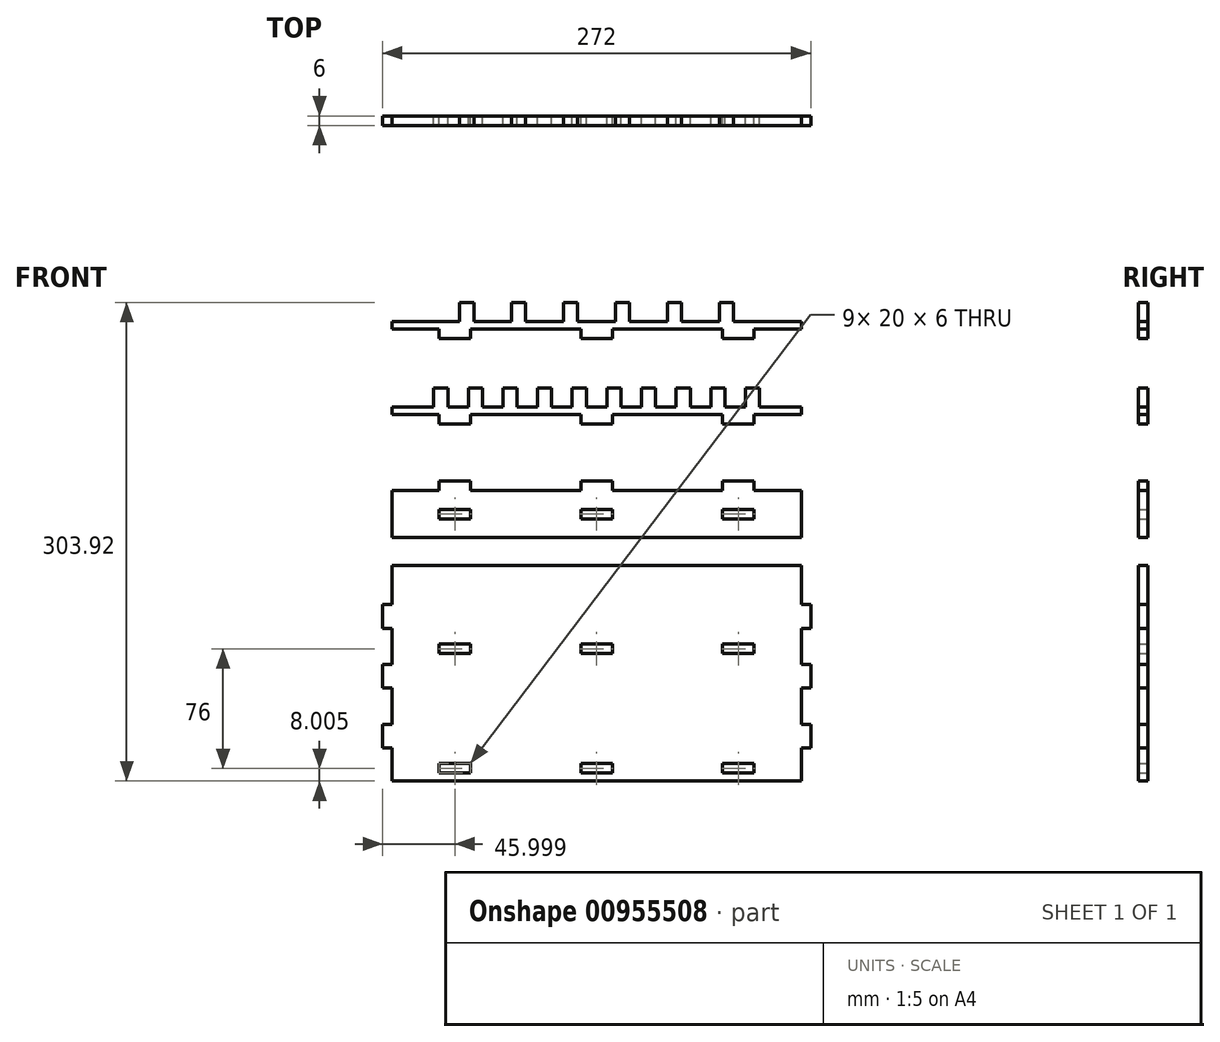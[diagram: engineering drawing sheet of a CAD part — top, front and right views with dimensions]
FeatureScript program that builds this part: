
annotation { "Feature Type Name" : "Feature", "Feature Type Description" : "" }
export const myFeature = defineFeature(function(context is Context, id is Id, definition is map)
    precondition{}
    {
        {
            var Q0;
            Q0=qCreatedBy(makeId("Front.planeOp"),FACE);
            var sketch = newSketch(context, id + "F0", { "sketchPlane" : qUnion([Q0])});
            skLineSegment(sketch, "E0", {"start": v(-63.3, 14.61) * mm, "end": v(-63.3, 26.61) * mm});
            skLineSegment(sketch, "E1", {"start": v(-63.3, 26.61) * mm, "end": v(-54.3, 26.61) * mm});
            skLineSegment(sketch, "E2", {"start": v(-54.3, 26.61) * mm, "end": v(-54.3, 14.61) * mm});
            skLineSegment(sketch, "E3", {"start": v(-54.3, 14.61) * mm, "end": v(-30.3, 14.61) * mm});
            skLineSegment(sketch, "E4.1.0.0", {"start": v(-30.3, 14.61) * mm, "end": v(-30.3, 26.61) * mm});
            skLineSegment(sketch, "E4.1.0.1", {"start": v(-30.3, 26.61) * mm, "end": v(-21.3, 26.61) * mm});
            skLineSegment(sketch, "E4.1.0.2", {"start": v(-21.3, 26.61) * mm, "end": v(-21.3, 14.61) * mm});
            skLineSegment(sketch, "E4.1.0.3", {"start": v(-21.3, 14.61) * mm, "end": v(2.7, 14.61) * mm});
            skLineSegment(sketch, "E4.2.0.0", {"start": v(2.7, 14.61) * mm, "end": v(2.7, 26.61) * mm});
            skLineSegment(sketch, "E4.2.0.1", {"start": v(2.7, 26.61) * mm, "end": v(11.7, 26.61) * mm});
            skLineSegment(sketch, "E4.2.0.2", {"start": v(11.7, 26.61) * mm, "end": v(11.7, 14.61) * mm});
            skLineSegment(sketch, "E4.2.0.3", {"start": v(11.7, 14.61) * mm, "end": v(35.7, 14.61) * mm});
            skLineSegment(sketch, "E4.3.0.0", {"start": v(35.7, 14.61) * mm, "end": v(35.7, 26.61) * mm});
            skLineSegment(sketch, "E4.3.0.1", {"start": v(35.7, 26.61) * mm, "end": v(44.7, 26.61) * mm});
            skLineSegment(sketch, "E4.3.0.2", {"start": v(44.7, 26.61) * mm, "end": v(44.7, 14.61) * mm});
            skLineSegment(sketch, "E4.direction1", {"start": v(-63.3, 14.61) * mm, "end": v(-30.3, 14.61) * mm, "construction": true});
            skLineSegment(sketch, "E5", {"start": v(-79.8, -39.65) * mm, "end": v(-79.8, -27.65) * mm});
            skLineSegment(sketch, "E6", {"start": v(-79.8, -27.65) * mm, "end": v(-70.8, -27.65) * mm});
            skLineSegment(sketch, "E7", {"start": v(-70.8, -27.65) * mm, "end": v(-70.8, -39.65) * mm});
            skLineSegment(sketch, "E8", {"start": v(-70.8, -39.65) * mm, "end": v(-57.8, -39.65) * mm});
            skLineSegment(sketch, "E9.1.0.0", {"start": v(-57.8, -39.65) * mm, "end": v(-57.8, -27.65) * mm});
            skLineSegment(sketch, "E9.1.0.1", {"start": v(-57.8, -27.65) * mm, "end": v(-48.8, -27.65) * mm});
            skLineSegment(sketch, "E9.1.0.2", {"start": v(-48.8, -27.65) * mm, "end": v(-48.8, -39.65) * mm});
            skLineSegment(sketch, "E9.1.0.3", {"start": v(-48.8, -39.65) * mm, "end": v(-35.8, -39.65) * mm});
            skLineSegment(sketch, "E9.2.0.0", {"start": v(-35.8, -39.65) * mm, "end": v(-35.8, -27.65) * mm});
            skLineSegment(sketch, "E9.2.0.1", {"start": v(-35.8, -27.65) * mm, "end": v(-26.8, -27.65) * mm});
            skLineSegment(sketch, "E9.2.0.2", {"start": v(-26.8, -27.65) * mm, "end": v(-26.8, -39.65) * mm});
            skLineSegment(sketch, "E9.2.0.3", {"start": v(-26.8, -39.65) * mm, "end": v(-13.8, -39.65) * mm});
            skLineSegment(sketch, "E9.direction1", {"start": v(-79.8, -39.65) * mm, "end": v(-57.8, -39.65) * mm, "construction": true});
            skLineSegment(sketch, "E10", {"start": v(-63.3, 14.61) * mm, "end": v(-106.3, 14.61) * mm});
            skLineSegment(sketch, "E11", {"start": v(-106.3, 14.61) * mm, "end": v(-106.3, 9.61) * mm});
            skLineSegment(sketch, "E12", {"start": v(-106.3, 9.61) * mm, "end": v(-76.3, 9.61) * mm});
            skLineSegment(sketch, "E13", {"start": v(-79.8, -39.65) * mm, "end": v(-106.3, -39.65) * mm});
            skLineSegment(sketch, "E14", {"start": v(-106.3, -39.65) * mm, "end": v(-106.3, -44.65) * mm});
            skLineSegment(sketch, "E15", {"start": v(-106.3, -44.65) * mm, "end": v(-76.3, -44.65) * mm});
            skLineSegment(sketch, "E16.top", {"start": v(-76.3, 3.61) * mm, "end": v(-56.3, 3.61) * mm});
            skLineSegment(sketch, "E16.left", {"start": v(-76.3, 9.61) * mm, "end": v(-76.3, 3.61) * mm});
            skLineSegment(sketch, "E16.right", {"start": v(-56.3, 9.61) * mm, "end": v(-56.3, 3.61) * mm});
            skLineSegment(sketch, "E17.top", {"start": v(-76.3, -50.65) * mm, "end": v(-56.3, -50.65) * mm});
            skLineSegment(sketch, "E17.left", {"start": v(-76.3, -44.65) * mm, "end": v(-76.3, -50.65) * mm});
            skLineSegment(sketch, "E17.right", {"start": v(-56.3, -44.65) * mm, "end": v(-56.3, -50.65) * mm});
            skLineSegment(sketch, "E18.1.0.0", {"start": v(13.7, 9.61) * mm, "end": v(13.7, 3.61) * mm});
            skLineSegment(sketch, "E18.1.0.1", {"start": v(13.7, 3.61) * mm, "end": v(33.7, 3.61) * mm});
            skLineSegment(sketch, "E18.1.0.2", {"start": v(33.7, 9.61) * mm, "end": v(33.7, 3.61) * mm});
            skLineSegment(sketch, "E18.2.0.0", {"start": v(103.7, 9.61) * mm, "end": v(103.7, 3.61) * mm});
            skLineSegment(sketch, "E18.2.0.1", {"start": v(103.7, 3.61) * mm, "end": v(123.7, 3.61) * mm});
            skLineSegment(sketch, "E18.2.0.2", {"start": v(123.7, 9.61) * mm, "end": v(123.7, 3.61) * mm});
            skLineSegment(sketch, "E18.direction1", {"start": v(-76.3, 3.61) * mm, "end": v(13.7, 3.61) * mm, "construction": true});
            skLineSegment(sketch, "E19.1.0.0", {"start": v(13.7, -44.65) * mm, "end": v(13.7, -50.65) * mm});
            skLineSegment(sketch, "E19.1.0.1", {"start": v(13.7, -50.65) * mm, "end": v(33.7, -50.65) * mm});
            skLineSegment(sketch, "E19.1.0.2", {"start": v(33.7, -44.65) * mm, "end": v(33.7, -50.65) * mm});
            skLineSegment(sketch, "E19.2.0.0", {"start": v(103.7, -44.65) * mm, "end": v(103.7, -50.65) * mm});
            skLineSegment(sketch, "E19.2.0.1", {"start": v(103.7, -50.65) * mm, "end": v(123.7, -50.65) * mm});
            skLineSegment(sketch, "E19.2.0.2", {"start": v(123.7, -44.65) * mm, "end": v(123.7, -50.65) * mm});
            skLineSegment(sketch, "E19.direction1", {"start": v(-76.3, -50.65) * mm, "end": v(13.7, -50.65) * mm, "construction": true});
            skLineSegment(sketch, "E20.trimOffspring", {"start": v(-56.3, 9.61) * mm, "end": v(13.7, 9.61) * mm});
            skLineSegment(sketch, "E21.trimOffspring", {"start": v(33.7, 9.61) * mm, "end": v(103.7, 9.61) * mm});
            skLineSegment(sketch, "E22.trimOffspring", {"start": v(33.7, -44.65) * mm, "end": v(103.7, -44.65) * mm});
            skLineSegment(sketch, "E23.trimOffspring", {"start": v(-56.3, -44.65) * mm, "end": v(13.7, -44.65) * mm});
            skLineSegment(sketch, "E24.bottom", {"start": v(-106.3, -92.77) * mm, "end": v(-76.3, -92.77) * mm});
            skLineSegment(sketch, "E24.top", {"start": v(-106.3, -122.77) * mm, "end": v(153.7, -122.77) * mm});
            skLineSegment(sketch, "E24.left", {"start": v(-106.3, -92.77) * mm, "end": v(-106.3, -122.77) * mm});
            skLineSegment(sketch, "E24.right", {"start": v(153.7, -92.77) * mm, "end": v(153.7, -122.77) * mm});
            skLineSegment(sketch, "E25", {"start": v(-106.3, -107.77) * mm, "end": v(153.7, -107.77) * mm, "construction": true});
            skLineSegment(sketch, "E26.bottom", {"start": v(-76.3, -104.77) * mm, "end": v(-56.3, -104.77) * mm});
            skLineSegment(sketch, "E26.top", {"start": v(-76.3, -110.77) * mm, "end": v(-56.3, -110.77) * mm});
            skLineSegment(sketch, "E26.left", {"start": v(-76.3, -104.77) * mm, "end": v(-76.3, -110.77) * mm});
            skLineSegment(sketch, "E26.right", {"start": v(-56.3, -104.77) * mm, "end": v(-56.3, -110.77) * mm});
            skPoint(sketch, "E26.middle", {"position": v(-66.3, -107.77) * mm});
            skLineSegment(sketch, "E27.1.0.0", {"start": v(13.7, -104.77) * mm, "end": v(33.7, -104.77) * mm});
            skLineSegment(sketch, "E27.1.0.1", {"start": v(13.7, -104.77) * mm, "end": v(13.7, -110.77) * mm});
            skLineSegment(sketch, "E27.1.0.2", {"start": v(13.7, -110.77) * mm, "end": v(33.7, -110.77) * mm});
            skLineSegment(sketch, "E27.1.0.3", {"start": v(33.7, -104.77) * mm, "end": v(33.7, -110.77) * mm});
            skLineSegment(sketch, "E27.2.0.0", {"start": v(103.7, -104.77) * mm, "end": v(123.7, -104.77) * mm});
            skLineSegment(sketch, "E27.2.0.1", {"start": v(103.7, -104.77) * mm, "end": v(103.7, -110.77) * mm});
            skLineSegment(sketch, "E27.2.0.2", {"start": v(103.7, -110.77) * mm, "end": v(123.7, -110.77) * mm});
            skLineSegment(sketch, "E27.2.0.3", {"start": v(123.7, -104.77) * mm, "end": v(123.7, -110.77) * mm});
            skLineSegment(sketch, "E27.direction1", {"start": v(-76.3, -104.77) * mm, "end": v(13.7, -104.77) * mm, "construction": true});
            skLineSegment(sketch, "E28.top", {"start": v(-76.3, -86.77) * mm, "end": v(-56.3, -86.77) * mm});
            skLineSegment(sketch, "E28.left", {"start": v(-76.3, -92.77) * mm, "end": v(-76.3, -86.77) * mm});
            skLineSegment(sketch, "E28.right", {"start": v(-56.3, -92.77) * mm, "end": v(-56.3, -86.77) * mm});
            skLineSegment(sketch, "E29.trimOffspring", {"start": v(-56.3, -92.77) * mm, "end": v(13.7, -92.77) * mm});
            skLineSegment(sketch, "E30.bottom", {"start": v(-106.3, -140.3) * mm, "end": v(153.7, -140.3) * mm});
            skLineSegment(sketch, "E30.top", {"start": v(-106.3, -277.3) * mm, "end": v(153.7, -277.3) * mm});
            skLineSegment(sketch, "E30.left", {"start": v(-106.3, -140.3) * mm, "end": v(-106.3, -165.3) * mm});
            skLineSegment(sketch, "E30.right", {"start": v(153.7, -140.3) * mm, "end": v(153.7, -165.3) * mm});
            skLineSegment(sketch, "E31", {"start": v(-106.3, -193.3) * mm, "end": v(153.7, -193.3) * mm, "construction": true});
            skLineSegment(sketch, "E32", {"start": v(-106.3, -269.3) * mm, "end": v(153.7, -269.3) * mm, "construction": true});
            skLineSegment(sketch, "E33.bottom", {"start": v(-56.3, -196.3) * mm, "end": v(-76.3, -196.3) * mm});
            skLineSegment(sketch, "E33.top", {"start": v(-56.3, -190.3) * mm, "end": v(-76.3, -190.3) * mm});
            skLineSegment(sketch, "E33.left", {"start": v(-56.3, -196.3) * mm, "end": v(-56.3, -190.3) * mm});
            skLineSegment(sketch, "E33.right", {"start": v(-76.3, -196.3) * mm, "end": v(-76.3, -190.3) * mm});
            skPoint(sketch, "E33.middle", {"position": v(-66.3, -193.3) * mm});
            skLineSegment(sketch, "E34.bottom", {"start": v(-56.3, -266.3) * mm, "end": v(-76.3, -266.3) * mm});
            skLineSegment(sketch, "E34.top", {"start": v(-56.3, -272.3) * mm, "end": v(-76.3, -272.3) * mm});
            skLineSegment(sketch, "E34.left", {"start": v(-56.3, -266.3) * mm, "end": v(-56.3, -272.3) * mm});
            skLineSegment(sketch, "E34.right", {"start": v(-76.3, -266.3) * mm, "end": v(-76.3, -272.3) * mm});
            skPoint(sketch, "E34.middle", {"position": v(-66.3, -269.3) * mm});
            skLineSegment(sketch, "E35.1.0.0", {"start": v(33.7, -190.3) * mm, "end": v(13.7, -190.3) * mm});
            skLineSegment(sketch, "E35.1.0.1", {"start": v(13.7, -196.3) * mm, "end": v(13.7, -190.3) * mm});
            skLineSegment(sketch, "E35.1.0.2", {"start": v(33.7, -196.3) * mm, "end": v(13.7, -196.3) * mm});
            skLineSegment(sketch, "E35.1.0.3", {"start": v(33.7, -196.3) * mm, "end": v(33.7, -190.3) * mm});
            skLineSegment(sketch, "E35.2.0.0", {"start": v(123.7, -190.3) * mm, "end": v(103.7, -190.3) * mm});
            skLineSegment(sketch, "E35.2.0.1", {"start": v(103.7, -196.3) * mm, "end": v(103.7, -190.3) * mm});
            skLineSegment(sketch, "E35.2.0.2", {"start": v(123.7, -196.3) * mm, "end": v(103.7, -196.3) * mm});
            skLineSegment(sketch, "E35.2.0.3", {"start": v(123.7, -196.3) * mm, "end": v(123.7, -190.3) * mm});
            skLineSegment(sketch, "E35.direction1", {"start": v(-76.3, -190.3) * mm, "end": v(13.7, -190.3) * mm, "construction": true});
            skLineSegment(sketch, "E36.1.0.0", {"start": v(13.7, -266.3) * mm, "end": v(13.7, -272.3) * mm});
            skLineSegment(sketch, "E36.1.0.1", {"start": v(33.7, -266.3) * mm, "end": v(13.7, -266.3) * mm});
            skLineSegment(sketch, "E36.1.0.2", {"start": v(33.7, -266.3) * mm, "end": v(33.7, -272.3) * mm});
            skLineSegment(sketch, "E36.1.0.3", {"start": v(33.7, -272.3) * mm, "end": v(13.7, -272.3) * mm});
            skLineSegment(sketch, "E36.2.0.0", {"start": v(103.7, -266.3) * mm, "end": v(103.7, -272.3) * mm});
            skLineSegment(sketch, "E36.2.0.1", {"start": v(123.7, -266.3) * mm, "end": v(103.7, -266.3) * mm});
            skLineSegment(sketch, "E36.2.0.2", {"start": v(123.7, -266.3) * mm, "end": v(123.7, -272.3) * mm});
            skLineSegment(sketch, "E36.2.0.3", {"start": v(123.7, -272.3) * mm, "end": v(103.7, -272.3) * mm});
            skLineSegment(sketch, "E36.direction1", {"start": v(-76.3, -272.3) * mm, "end": v(13.7, -272.3) * mm, "construction": true});
            skLineSegment(sketch, "E37.bottom", {"start": v(-106.3, -165.3) * mm, "end": v(-112.3, -165.3) * mm});
            skLineSegment(sketch, "E37.top", {"start": v(-106.3, -180.3) * mm, "end": v(-112.3, -180.3) * mm});
            skLineSegment(sketch, "E37.right", {"start": v(-112.3, -165.3) * mm, "end": v(-112.3, -180.3) * mm});
            skLineSegment(sketch, "E38.0.1.0", {"start": v(-106.3, -203.3) * mm, "end": v(-112.3, -203.3) * mm});
            skLineSegment(sketch, "E38.0.1.2", {"start": v(-106.3, -218.3) * mm, "end": v(-112.3, -218.3) * mm});
            skLineSegment(sketch, "E38.0.1.3", {"start": v(-112.3, -203.3) * mm, "end": v(-112.3, -218.3) * mm});
            skLineSegment(sketch, "E38.1.0.0", {"start": v(159.7, -165.3) * mm, "end": v(153.7, -165.3) * mm});
            skLineSegment(sketch, "E38.1.0.1", {"start": v(159.7, -165.3) * mm, "end": v(159.7, -180.3) * mm});
            skLineSegment(sketch, "E38.1.0.2", {"start": v(159.7, -180.3) * mm, "end": v(153.7, -180.3) * mm});
            skLineSegment(sketch, "E38.1.1.0", {"start": v(159.7, -203.3) * mm, "end": v(153.7, -203.3) * mm});
            skLineSegment(sketch, "E38.1.1.1", {"start": v(159.7, -203.3) * mm, "end": v(159.7, -218.3) * mm});
            skLineSegment(sketch, "E38.1.1.2", {"start": v(159.7, -218.3) * mm, "end": v(153.7, -218.3) * mm});
            skLineSegment(sketch, "E38.direction1", {"start": v(-112.3, -165.3) * mm, "end": v(153.7, -165.3) * mm, "construction": true});
            skLineSegment(sketch, "E38.direction2", {"start": v(-112.3, -165.3) * mm, "end": v(-112.3, -203.3) * mm, "construction": true});
            skLineSegment(sketch, "E39.trimOffspring", {"start": v(-106.3, -218.3) * mm, "end": v(-106.3, -241.3) * mm});
            skLineSegment(sketch, "E40.trimOffspring", {"start": v(153.7, -180.3) * mm, "end": v(153.7, -203.3) * mm});
            skLineSegment(sketch, "E41.trimOffspring", {"start": v(153.7, -218.3) * mm, "end": v(153.7, -241.3) * mm});
            skLineSegment(sketch, "E42.trimOffspring", {"start": v(-106.3, -180.3) * mm, "end": v(-106.3, -203.3) * mm});
            skLineSegment(sketch, "E43.0.3.0", {"start": v(-13.8, -39.65) * mm, "end": v(-13.8, -27.65) * mm});
            skLineSegment(sketch, "E43.3.3.0", {"start": v(-13.8, -27.65) * mm, "end": v(-4.8, -27.65) * mm});
            skLineSegment(sketch, "E43.6.3.0", {"start": v(-4.8, -27.65) * mm, "end": v(-4.8, -39.65) * mm});
            skLineSegment(sketch, "E43.9.3.0", {"start": v(-4.8, -39.65) * mm, "end": v(8.2, -39.65) * mm});
            skLineSegment(sketch, "E43.0.4.0", {"start": v(8.2, -39.65) * mm, "end": v(8.2, -27.65) * mm});
            skLineSegment(sketch, "E43.3.4.0", {"start": v(8.2, -27.65) * mm, "end": v(17.2, -27.65) * mm});
            skLineSegment(sketch, "E43.6.4.0", {"start": v(17.2, -27.65) * mm, "end": v(17.2, -39.65) * mm});
            skLineSegment(sketch, "E43.9.4.0", {"start": v(17.2, -39.65) * mm, "end": v(30.2, -39.65) * mm});
            skLineSegment(sketch, "E43.0.5.0", {"start": v(30.2, -39.65) * mm, "end": v(30.2, -27.65) * mm});
            skLineSegment(sketch, "E43.3.5.0", {"start": v(30.2, -27.65) * mm, "end": v(39.2, -27.65) * mm});
            skLineSegment(sketch, "E43.6.5.0", {"start": v(39.2, -27.65) * mm, "end": v(39.2, -39.65) * mm});
            skLineSegment(sketch, "E43.9.5.0", {"start": v(39.2, -39.65) * mm, "end": v(52.2, -39.65) * mm});
            skLineSegment(sketch, "E43.0.6.0", {"start": v(52.2, -39.65) * mm, "end": v(52.2, -27.65) * mm});
            skLineSegment(sketch, "E43.3.6.0", {"start": v(52.2, -27.65) * mm, "end": v(61.2, -27.65) * mm});
            skLineSegment(sketch, "E43.6.6.0", {"start": v(61.2, -27.65) * mm, "end": v(61.2, -39.65) * mm});
            skLineSegment(sketch, "E44", {"start": v(123.7, -44.65) * mm, "end": v(153.7, -44.65) * mm});
            skLineSegment(sketch, "E45", {"start": v(153.7, -44.65) * mm, "end": v(153.7, -39.65) * mm});
            skLineSegment(sketch, "E46", {"start": v(153.7, 14.61) * mm, "end": v(153.7, 9.61) * mm});
            skLineSegment(sketch, "E47", {"start": v(153.7, 9.61) * mm, "end": v(123.7, 9.61) * mm});
            skLineSegment(sketch, "E48.1.0.0", {"start": v(13.7, -92.77) * mm, "end": v(13.7, -86.77) * mm});
            skLineSegment(sketch, "E48.1.0.1", {"start": v(13.7, -86.77) * mm, "end": v(33.7, -86.77) * mm});
            skLineSegment(sketch, "E48.1.0.2", {"start": v(33.7, -92.77) * mm, "end": v(33.7, -86.77) * mm});
            skLineSegment(sketch, "E48.2.0.0", {"start": v(103.7, -92.77) * mm, "end": v(103.7, -86.77) * mm});
            skLineSegment(sketch, "E48.2.0.1", {"start": v(103.7, -86.77) * mm, "end": v(123.7, -86.77) * mm});
            skLineSegment(sketch, "E48.2.0.2", {"start": v(123.7, -92.77) * mm, "end": v(123.7, -86.77) * mm});
            skLineSegment(sketch, "E48.direction1", {"start": v(-76.3, -92.77) * mm, "end": v(13.7, -92.77) * mm, "construction": true});
            skLineSegment(sketch, "E49.trimOffspring", {"start": v(33.7, -92.77) * mm, "end": v(103.7, -92.77) * mm});
            skLineSegment(sketch, "E50.trimOffspring", {"start": v(123.7, -92.77) * mm, "end": v(153.7, -92.77) * mm});
            skLineSegment(sketch, "E51.0.4.0", {"start": v(68.7, 14.61) * mm, "end": v(68.7, 26.61) * mm});
            skLineSegment(sketch, "E51.3.4.0", {"start": v(68.7, 26.61) * mm, "end": v(77.7, 26.61) * mm});
            skLineSegment(sketch, "E51.6.4.0", {"start": v(77.7, 26.61) * mm, "end": v(77.7, 14.61) * mm});
            skLineSegment(sketch, "E51.9.4.0", {"start": v(77.7, 14.61) * mm, "end": v(101.7, 14.61) * mm});
            skLineSegment(sketch, "E51.0.5.0", {"start": v(101.7, 14.61) * mm, "end": v(101.7, 26.61) * mm});
            skLineSegment(sketch, "E51.3.5.0", {"start": v(101.7, 26.61) * mm, "end": v(110.7, 26.61) * mm});
            skLineSegment(sketch, "E51.6.5.0", {"start": v(110.7, 26.61) * mm, "end": v(110.7, 14.61) * mm});
            skLineSegment(sketch, "E51.9.5.0", {"start": v(110.7, 14.61) * mm, "end": v(134.7, 14.61) * mm});
            skLineSegment(sketch, "E52.0.7.0", {"start": v(74.2, -39.65) * mm, "end": v(74.2, -27.65) * mm});
            skLineSegment(sketch, "E52.3.7.0", {"start": v(74.2, -27.65) * mm, "end": v(83.2, -27.65) * mm});
            skLineSegment(sketch, "E52.6.7.0", {"start": v(83.2, -27.65) * mm, "end": v(83.2, -39.65) * mm});
            skLineSegment(sketch, "E52.9.7.0", {"start": v(83.2, -39.65) * mm, "end": v(96.2, -39.65) * mm});
            skLineSegment(sketch, "E52.0.8.0", {"start": v(96.2, -39.65) * mm, "end": v(96.2, -27.65) * mm});
            skLineSegment(sketch, "E52.3.8.0", {"start": v(96.2, -27.65) * mm, "end": v(105.2, -27.65) * mm});
            skLineSegment(sketch, "E52.6.8.0", {"start": v(105.2, -27.65) * mm, "end": v(105.2, -39.65) * mm});
            skLineSegment(sketch, "E52.9.8.0", {"start": v(105.2, -39.65) * mm, "end": v(118.2, -39.65) * mm});
            skLineSegment(sketch, "E52.0.9.0", {"start": v(118.2, -39.65) * mm, "end": v(118.2, -27.65) * mm});
            skLineSegment(sketch, "E52.3.9.0", {"start": v(118.2, -27.65) * mm, "end": v(127.2, -27.65) * mm});
            skLineSegment(sketch, "E52.6.9.0", {"start": v(127.2, -27.65) * mm, "end": v(127.2, -39.65) * mm});
            skLineSegment(sketch, "E52.9.9.0", {"start": v(127.2, -39.65) * mm, "end": v(140.2, -39.65) * mm});
            skLineSegment(sketch, "E53", {"start": v(134.7, 14.61) * mm, "end": v(153.7, 14.61) * mm});
            skLineSegment(sketch, "E54", {"start": v(140.2, -39.65) * mm, "end": v(153.7, -39.65) * mm});
            skLineSegment(sketch, "E55", {"start": v(44.7, 14.61) * mm, "end": v(68.7, 14.61) * mm});
            skLineSegment(sketch, "E56", {"start": v(61.2, -39.65) * mm, "end": v(74.2, -39.65) * mm});
            skLineSegment(sketch, "E57.0.0.2", {"start": v(-106.3, -241.3) * mm, "end": v(-112.3, -241.3) * mm});
            skLineSegment(sketch, "E57.6.0.2", {"start": v(-106.3, -256.3) * mm, "end": v(-112.3, -256.3) * mm});
            skLineSegment(sketch, "E57.9.0.2", {"start": v(-112.3, -241.3) * mm, "end": v(-112.3, -256.3) * mm});
            skLineSegment(sketch, "E57.0.1.2", {"start": v(159.7, -241.3) * mm, "end": v(153.7, -241.3) * mm});
            skLineSegment(sketch, "E57.3.1.2", {"start": v(159.7, -241.3) * mm, "end": v(159.7, -256.3) * mm});
            skLineSegment(sketch, "E57.6.1.2", {"start": v(159.7, -256.3) * mm, "end": v(153.7, -256.3) * mm});
            skLineSegment(sketch, "E58.trimOffspring", {"start": v(-106.3, -256.3) * mm, "end": v(-106.3, -277.3) * mm});
            skLineSegment(sketch, "E59.trimOffspring", {"start": v(153.7, -256.3) * mm, "end": v(153.7, -277.3) * mm});
            skSolve(sketch);
        }
        {
            var Q0;
            Q0=makeQuery(id+"F0.imprint","IMPRINT",FACE,{"disambiguationData":[TD([[makeQuery(id+"F0.imprint","IMPRINT",EDGE,{"derivedFrom":sQuery(id+"F0.wireOp",EDGE,"E30.bottom")}),-1.0]])]});
            extrude(context, id + "F1", {"entities" : qUnion([Q0]), "depth" : 6 * mm, "offsetDistance" : 25 * mm});
        }
        {
            var Q0;
            Q0=makeQuery(id+"F0.imprint","IMPRINT",FACE,{"disambiguationData":[TD([[makeQuery(id+"F0.imprint","IMPRINT",EDGE,{"derivedFrom":sQuery(id+"F0.wireOp",EDGE,"E24.bottom")}),-1.0]])]});
            extrude(context, id + "F2", {"entities" : qUnion([Q0]), "depth" : 6 * mm, "offsetDistance" : 25 * mm});
        }
        {
            var Q0;
            Q0=makeQuery(id+"F0.imprint","IMPRINT",FACE,{"disambiguationData":[TD([[makeQuery(id+"F0.imprint","IMPRINT",EDGE,{"derivedFrom":sQuery(id+"F0.wireOp",EDGE,"E0")}),-1.0]])]});
            extrude(context, id + "F3", {"entities" : qUnion([Q0]), "depth" : 6 * mm, "offsetDistance" : 25 * mm});
        }
        {
            var Q0;
            Q0=makeQuery(id+"F0.imprint","IMPRINT",FACE,{"disambiguationData":[TD([[makeQuery(id+"F0.imprint","IMPRINT",EDGE,{"derivedFrom":sQuery(id+"F0.wireOp",EDGE,"E5")}),-1.0]])]});
            var Q1;
            Q1=makeQuery(id+"F0.imprint","IMPRINT",FACE,{"disambiguationData":[TD([[makeQuery(id+"F0.imprint","IMPRINT",EDGE,{"derivedFrom":sQuery(id+"F0.wireOp",EDGE,"aaeb0c92-a25c-4613-a32c-7460083762f4")}),-1.0]])]});
            extrude(context, id + "F4", {"entities" : qUnion([Q0, Q1]), "depth" : 6 * mm, "offsetDistance" : 25 * mm});
        }
    });
